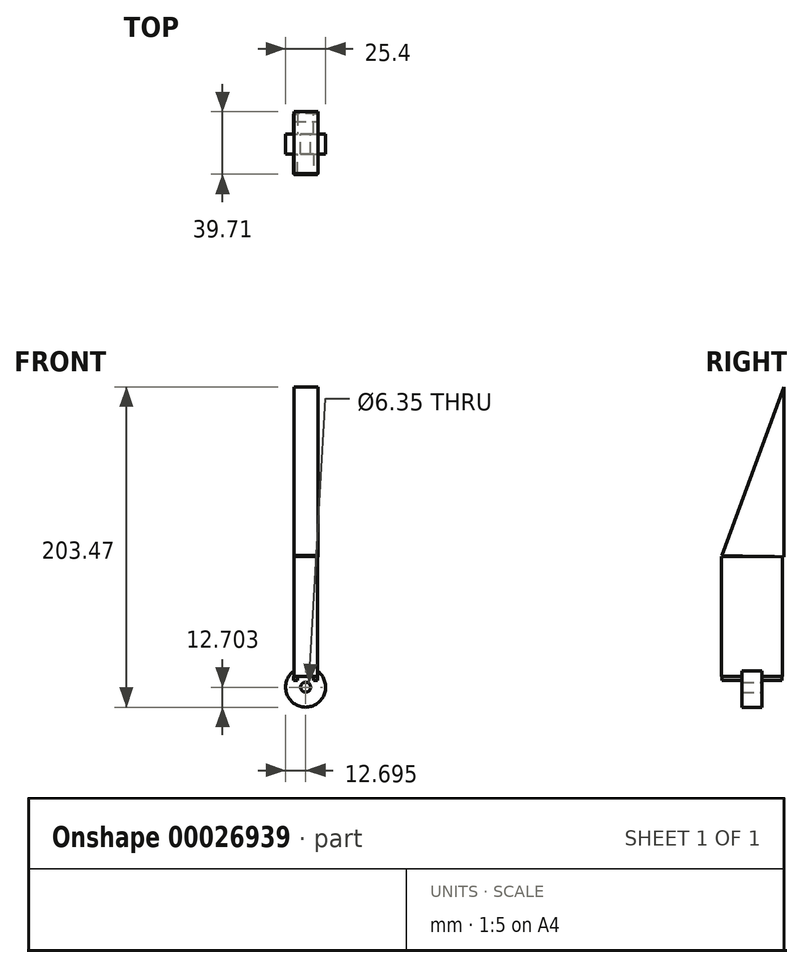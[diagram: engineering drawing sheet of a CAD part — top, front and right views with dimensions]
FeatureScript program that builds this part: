
annotation { "Feature Type Name" : "Feature", "Feature Type Description" : "" }
export const myFeature = defineFeature(function(context is Context, id is Id, definition is map)
    precondition{}
    {
        {
            var Q0;
            Q0=qCreatedBy(makeId("Front.planeOp"),FACE);
            var sketch = newSketch(context, id + "F0", { "sketchPlane" : qUnion([Q0])});
            skCircle(sketch, "E0", {"center": v(-47.92, 32.27) * mm, "radius": 12.7 * mm});
            skCircle(sketch, "E1", {"center": v(-47.92, 32.27) * mm, "radius": 3.18 * mm});
            skLineSegment(sketch, "E2.bottom", {"start": v(-55.51, 39.03) * mm, "end": v(-52.97, 39.03) * mm});
            skLineSegment(sketch, "E2.top", {"start": v(-55.51, 36.49) * mm, "end": v(-52.97, 36.49) * mm});
            skLineSegment(sketch, "E2.left", {"start": v(-55.51, 39.03) * mm, "end": v(-55.51, 36.49) * mm});
            skLineSegment(sketch, "E2.right", {"start": v(-52.97, 39.03) * mm, "end": v(-52.97, 36.49) * mm});
            skLineSegment(sketch, "E3.bottom", {"start": v(-42.98, 39.15) * mm, "end": v(-40.44, 39.15) * mm});
            skLineSegment(sketch, "E3.top", {"start": v(-42.98, 36.6) * mm, "end": v(-40.44, 36.6) * mm});
            skLineSegment(sketch, "E3.left", {"start": v(-42.98, 39.15) * mm, "end": v(-42.98, 36.6) * mm});
            skLineSegment(sketch, "E3.right", {"start": v(-40.44, 39.15) * mm, "end": v(-40.44, 36.6) * mm});
            skSolve(sketch);
        }
        {
            var Q0;
            Q0=makeQuery(id+"F0.imprint","IMPRINT",FACE,{"disambiguationData":[TD([[makeQuery(id+"F0.imprint","IMPRINT",EDGE,{"derivedFrom":sQuery(id+"F0.wireOp",EDGE,"E0")}),1.0]])]});
            extrude(context, id + "F1", {"entities" : qUnion([Q0]), "depth" : 12.7 * mm});
        }
        {
            var Q0;
            Q0=makeQuery(id+"F0.imprint","IMPRINT",FACE,{"disambiguationData":[TD([[makeQuery(id+"F0.imprint","IMPRINT",EDGE,{"derivedFrom":sQuery(id+"F0.wireOp",EDGE,"E2.bottom")}),-1.0]])]});
            extrude(context, id + "F2", {"entities" : qUnion([Q0]), "operationType" : NewBodyOperationType.ADD, "depth" : 25.4 * mm});
        }
        {
            var Q0;
            Q0=makeQuery(id+"F0.imprint","IMPRINT",FACE,{"disambiguationData":[TD([[makeQuery(id+"F0.imprint","IMPRINT",EDGE,{"derivedFrom":sQuery(id+"F0.wireOp",EDGE,"E2.bottom")}),-1.0]])]});
            extrude(context, id + "F3", {"entities" : qUnion([Q0]), "operationType" : NewBodyOperationType.ADD, "oppositeDirection" : true, "depth" : 12.7 * mm});
        }
        {
            var Q0;
            Q0=makeQuery(id+"F0.imprint","IMPRINT",FACE,{"disambiguationData":[TD([[makeQuery(id+"F0.imprint","IMPRINT",EDGE,{"derivedFrom":sQuery(id+"F0.wireOp",EDGE,"E3.bottom")}),-1.0]])]});
            extrude(context, id + "F4", {"entities" : qUnion([Q0]), "operationType" : NewBodyOperationType.ADD, "depth" : 25.4 * mm});
        }
        {
            var Q0;
            Q0=makeQuery(id+"F0.imprint","IMPRINT",FACE,{"disambiguationData":[TD([[makeQuery(id+"F0.imprint","IMPRINT",EDGE,{"derivedFrom":sQuery(id+"F0.wireOp",EDGE,"E3.bottom")}),-1.0]])]});
            extrude(context, id + "F5", {"entities" : qUnion([Q0]), "operationType" : NewBodyOperationType.ADD, "oppositeDirection" : true, "depth" : 12.7 * mm});
        }
        {
            var Q0;
            Q0=makeQuery(id+"F2.opExtrude","SWEPT_FACE",FACE,{"disambiguationData":[OSD([sQuery(id+"F0.wireOp",EDGE,"E2.bottom")])]});
            cPlane(context, id + "F6", {"entities" : qUnion([Q0]), "cplaneType" : CPlaneType.OFFSET, "offset" : 0 * mm, "width" : 152.4 * mm, "height" : 152.4 * mm});
        }
        {
            var Q0;
            Q0=qCreatedBy(id+"F6.planeOp",FACE);
            var sketch = newSketch(context, id + "F7", { "sketchPlane" : qUnion([Q0])});
            skLineSegment(sketch, "E4.bottom", {"start": v(-40.35, -25.66) * mm, "end": v(-55.31, -25.66) * mm});
            skLineSegment(sketch, "E4.top", {"start": v(-40.35, 12.85) * mm, "end": v(-55.31, 12.85) * mm});
            skLineSegment(sketch, "E4.left", {"start": v(-40.35, -25.66) * mm, "end": v(-40.35, 12.85) * mm});
            skLineSegment(sketch, "E4.right", {"start": v(-55.31, -25.66) * mm, "end": v(-55.31, 12.85) * mm});
            skSolve(sketch);
        }
        {
            var Q0;
            Q0=makeQuery(id+"F7.imprint","IMPRINT",FACE,{"disambiguationData":[TD([[makeQuery(id+"F7.imprint","IMPRINT",EDGE,{"derivedFrom":sQuery(id+"F7.wireOp",EDGE,"E4.bottom")}),-1.0]])]});
            extrude(context, id + "F8", {"entities" : qUnion([Q0]), "operationType" : NewBodyOperationType.ADD, "depth" : 76.2 * mm});
        }
        {
            var Q0;
            Q0=makeQuery(id+"F8.opExtrude","SWEPT_FACE",FACE,{"disambiguationData":[OSD([sQuery(id+"F7.wireOp",EDGE,"E4.right")])]});
            cPlane(context, id + "F9", {"entities" : qUnion([Q0]), "cplaneType" : CPlaneType.OFFSET, "offset" : 0 * mm, "width" : 152.4 * mm, "height" : 152.4 * mm});
        }
        {
            var Q0;
            Q0=qCreatedBy(id+"F9.planeOp",FACE);
            var sketch = newSketch(context, id + "F10", { "sketchPlane" : qUnion([Q0])});
            skLineSegment(sketch, "E5", {"start": v(-14.05, 115.08) * mm, "end": v(-14.05, 223.04) * mm});
            skLineSegment(sketch, "E6", {"start": v(-14.05, 223.04) * mm, "end": v(25.3, 116.03) * mm});
            skLineSegment(sketch, "E7", {"start": v(-14.05, 115.08) * mm, "end": v(25.3, 116.03) * mm});
            skSolve(sketch);
        }
        {
            var Q0;
            Q0=makeQuery(id+"F10.imprint","IMPRINT",FACE,{"disambiguationData":[TD([[makeQuery(id+"F10.imprint","IMPRINT",EDGE,{"derivedFrom":sQuery(id+"F10.wireOp",EDGE,"E5")}),-1.0]])]});
            extrude(context, id + "F11", {"entities" : qUnion([Q0]), "operationType" : NewBodyOperationType.ADD, "oppositeDirection" : true, "depth" : 15.24 * mm});
        }
    });
